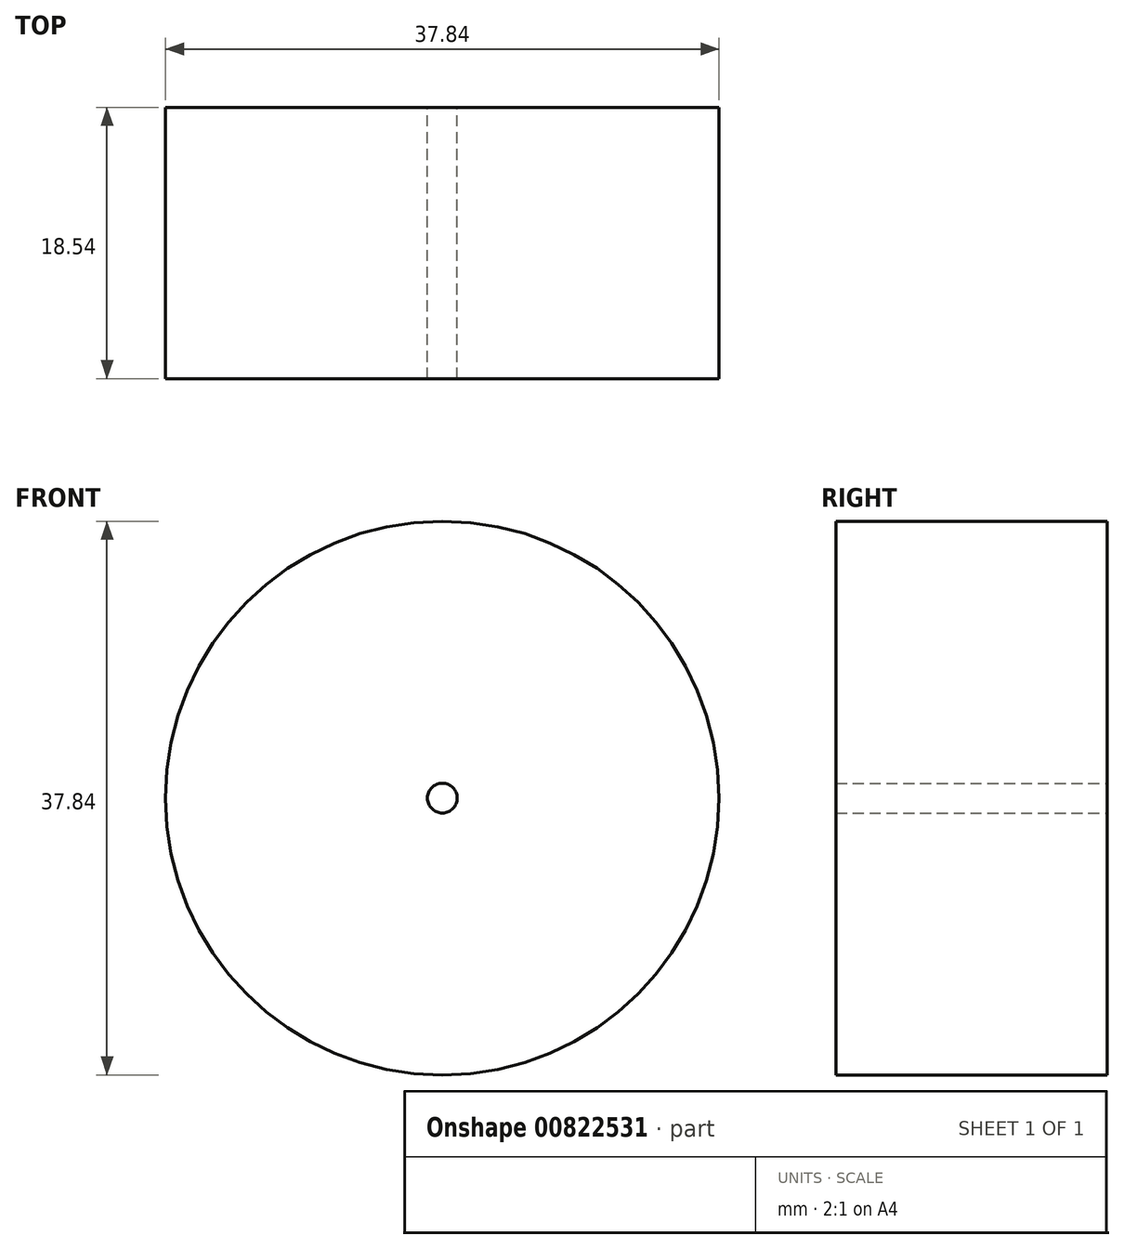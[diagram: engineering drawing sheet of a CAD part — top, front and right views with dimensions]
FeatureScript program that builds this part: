
annotation { "Feature Type Name" : "Feature", "Feature Type Description" : "" }
export const myFeature = defineFeature(function(context is Context, id is Id, definition is map)
    precondition{}
    {
        {
            var Q0;
            Q0=qCreatedBy(makeId("Front.planeOp"),FACE);
            var sketch = newSketch(context, id + "F0", { "sketchPlane" : qUnion([Q0])});
            skCircle(sketch, "E0", {"center": v(0, 0) * mm, "radius": 18.92 * mm});
            skCircle(sketch, "E1", {"center": v(0, 0) * mm, "radius": 1.02 * mm});
            skSolve(sketch);
        }
        {
            var Q0;
            Q0=makeQuery(id+"F0.imprint","IMPRINT",FACE,{"disambiguationData":[TD([[makeQuery(id+"F0.imprint","IMPRINT",EDGE,{"derivedFrom":sQuery(id+"F0.wireOp",EDGE,"E0")}),1.0]])]});
            extrude(context, id + "F1", {"entities" : qUnion([Q0]), "depth" : 18.54 * mm, "offsetDistance" : 25.4 * mm});
        }
    });
